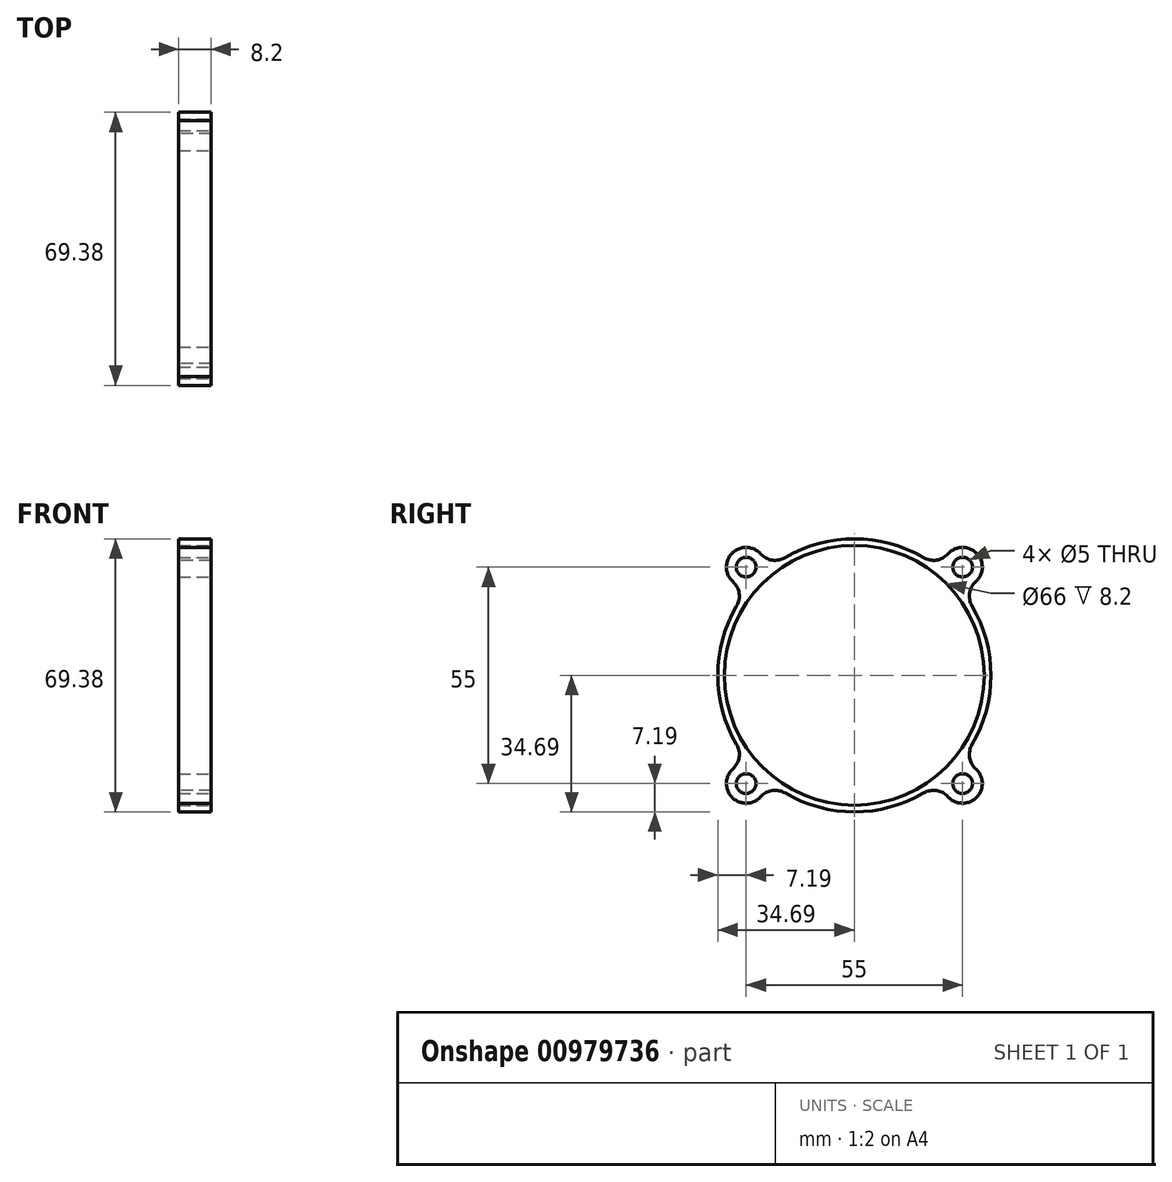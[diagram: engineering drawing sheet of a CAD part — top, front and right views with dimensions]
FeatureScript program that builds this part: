
annotation { "Feature Type Name" : "Feature", "Feature Type Description" : "" }
export const myFeature = defineFeature(function(context is Context, id is Id, definition is map)
    precondition{}
    {
        {
            var Q0;
            Q0=qCreatedBy(makeId("Front.planeOp"),FACE);
            var sketch = newSketch(context, id + "F0", { "sketchPlane" : qUnion([Q0])});
            skLineSegment(sketch, "E0.bottom", {"start": v(20, 40) * mm, "end": v(-20, 40) * mm});
            skLineSegment(sketch, "E0.top", {"start": v(20, -40) * mm, "end": v(-20, -40) * mm});
            skLineSegment(sketch, "E0.left", {"start": v(20, 40) * mm, "end": v(20, -40) * mm});
            skLineSegment(sketch, "E0.right", {"start": v(-20, 40) * mm, "end": v(-20, -40) * mm});
            skPoint(sketch, "E0.middle", {"position": v(0, 0) * mm});
            skSolve(sketch);
        }
        {
            var Q0;
            Q0=qSketchRegion(id+"F0",true);
            extrude(context, id + "F1", {"entities" : qUnion([Q0]), "depth" : 40 * mm, "offsetDistance" : 25 * mm, "hasSecondDirection" : true, "secondDirectionOppositeDirection" : true, "secondDirectionDepth" : 40 * mm});
        }
        {
            var Q0;
            Q0=qCreatedBy(makeId("Front.planeOp"),FACE);
            var sketch = newSketch(context, id + "F2", { "sketchPlane" : qUnion([Q0])});
            skLineSegment(sketch, "E1.left", {"start": v(-17.4, 25) * mm, "end": v(-17.4, 27.1) * mm});
            skPoint(sketch, "E2.center.orphan", {"position": v(0, -57) * mm});
            skPoint(sketch, "E3.start.orphan", {"position": v(-44.08, 0) * mm});
            skArc(sketch, "E4", {"start": v(13.13, 32.04) * mm, "mid": v(0, 33) * mm, "end": v(-13.13, 32.04) * mm});
            skLineSegment(sketch, "E5", {"start": v(17.4, 27.1) * mm, "end": v(17.4, 25) * mm});
            skArc(sketch, "E6", {"start": v(-13.13, 32.04) * mm, "mid": v(-16.18, 30.36) * mm, "end": v(-17.4, 27.1) * mm});
            skArc(sketch, "E7", {"start": v(17.4, 27.1) * mm, "mid": v(16.18, 30.36) * mm, "end": v(13.13, 32.04) * mm});
            skLineSegment(sketch, "E8", {"start": v(-44.08, 0) * mm, "end": v(-17.4, 0) * mm, "construction": true});
            skPoint(sketch, "E9.middle", {"position": v(0, 0) * mm});
            skPoint(sketch, "E9.top.end.orphan", {"position": v(-12.4, -25) * mm});
            skPoint(sketch, "E10.orphan", {"position": v(12.4, -25) * mm});
            skLineSegment(sketch, "E11.trimOffspring", {"start": v(17.4, 0) * mm, "end": v(38.47, 0) * mm, "construction": true});
            skPoint(sketch, "E12.start.orphan", {"position": v(-12.4, 25) * mm});
            skPoint(sketch, "E13.start.orphan", {"position": v(12.4, 25) * mm});
            skLineSegment(sketch, "E14", {"start": v(-17.4, 0) * mm, "end": v(17.4, 0) * mm});
            skLineSegment(sketch, "E15.bottom", {"start": v(-38.47, 25) * mm, "end": v(38.47, 25) * mm});
            skLineSegment(sketch, "E15.left", {"start": v(-38.47, 25) * mm, "end": v(-38.47, 0) * mm});
            skLineSegment(sketch, "E15.right", {"start": v(38.47, 25) * mm, "end": v(38.47, 0) * mm});
            skLineSegment(sketch, "E16", {"start": v(-38.47, 0) * mm, "end": v(38.47, 0) * mm});
            skPoint(sketch, "E15.top.start.orphan", {"position": v(-38.47, -25) * mm});
            skPoint(sketch, "E17.orphan", {"position": v(38.47, -25) * mm});
            skSolve(sketch);
        }
        {
            var Q0;
            Q0=qSketchRegion(id+"F2",true);
            var Q1;
            Q1=sQuery(id+"F2.wireOp",EDGE,"E8");
            revolve(context, id + "F3", {"operationType" : NewBodyOperationType.REMOVE, "surfaceOperationType" : NewSurfaceOperationType.NEW, "entities" : qUnion([Q0]), "axis" : qUnion([Q1]), "revolveType" : RevolveType.FULL});
        }
        {
            var Q0;
            Q0=makeQuery(id+"F1.opExtrude","SWEPT_FACE",FACE,{"disambiguationData":[OSD([sQuery(id+"F0.wireOp",EDGE,"E0.left")])]});
            var sketch = newSketch(context, id + "F4", { "sketchPlane" : qUnion([Q0])});
            skArc(sketch, "E18", {"start": v(-26.27, -22.65) * mm, "mid": v(-31.04, -31.04) * mm, "end": v(-22.65, -26.27) * mm});
            skArc(sketch, "E19", {"start": v(-22.65, 26.27) * mm, "mid": v(-31.04, 31.04) * mm, "end": v(-26.27, 22.65) * mm});
            skArc(sketch, "E20", {"start": v(26.27, 22.65) * mm, "mid": v(31.04, 31.04) * mm, "end": v(22.65, 26.27) * mm});
            skArc(sketch, "E21", {"start": v(22.65, -26.27) * mm, "mid": v(31.04, -31.04) * mm, "end": v(26.27, -22.65) * mm});
            skArc(sketch, "E22", {"start": v(-22.65, -26.27) * mm, "mid": v(0, -34.69) * mm, "end": v(22.65, -26.27) * mm});
            skArc(sketch, "E23.trimOffspring", {"start": v(-26.27, 22.65) * mm, "mid": v(-34.69, 0) * mm, "end": v(-26.27, -22.65) * mm});
            skArc(sketch, "E24.trimOffspring", {"start": v(22.65, 26.27) * mm, "mid": v(0, 34.69) * mm, "end": v(-22.65, 26.27) * mm});
            skArc(sketch, "E25.trimOffspring", {"start": v(26.27, -22.65) * mm, "mid": v(34.69, 0) * mm, "end": v(26.27, 22.65) * mm});
            skCircle(sketch, "E26", {"center": v(0, 0) * mm, "radius": 64.28 * mm});
            skSolve(sketch);
        }
        {
            var Q0;
            Q0=qSketchRegion(id+"F4",true);
            extrude(context, id + "F5", {"entities" : qUnion([Q0]), "operationType" : NewBodyOperationType.REMOVE, "oppositeDirection" : true, "depth" : 40 * mm, "offsetDistance" : 25 * mm});
        }
        {
            var Q0;
            Q0=makeQuery(id+"F5.boolean.opBoolean","MERGE",FACE,{"derivedFrom":[makeQuery(id+"F1.opExtrude","SWEPT_FACE",FACE,{"disambiguationData":[OSD([sQuery(id+"F0.wireOp",EDGE,"E0.left")])]}),makeQuery(id+"F5.opExtrude","CAP_FACE",FACE,{"disambiguationData":[OSD([sQuery(id+"F4.wireOp",EDGE,"E18")])],"isStart":true}),makeQuery(id+"F5.opExtrude","CAP_FACE",FACE,{"disambiguationData":[OSD([sQuery(id+"F4.wireOp",EDGE,"E19")])],"isStart":true}),makeQuery(id+"F5.opExtrude","CAP_FACE",FACE,{"disambiguationData":[OSD([sQuery(id+"F4.wireOp",EDGE,"E20")])],"isStart":true}),makeQuery(id+"F5.opExtrude","CAP_FACE",FACE,{"disambiguationData":[OSD([sQuery(id+"F4.wireOp",EDGE,"E21")])],"isStart":true})]});
            var sketch = newSketch(context, id + "F6", { "sketchPlane" : qUnion([Q0])});
            skCircle(sketch, "E27", {"center": v(-27.5, 27.5) * mm, "radius": 2.5 * mm});
            skCircle(sketch, "E28", {"center": v(27.5, 27.5) * mm, "radius": 2.5 * mm});
            skCircle(sketch, "E29", {"center": v(-27.5, -27.5) * mm, "radius": 2.5 * mm});
            skCircle(sketch, "E30", {"center": v(27.5, -27.5) * mm, "radius": 2.5 * mm});
            skSolve(sketch);
        }
        {
            var Q0;
            Q0=qSketchRegion(id+"F6",true);
            extrude(context, id + "F7", {"entities" : qUnion([Q0]), "operationType" : NewBodyOperationType.REMOVE, "endBound" : BoundingType.THROUGH_ALL, "oppositeDirection" : true, "depth" : 25 * mm, "offsetDistance" : 25 * mm});
        }
        {
            var Q0;
            Q0=qCreatedBy(makeId("Right.planeOp"),FACE);
            var sketch = newSketch(context, id + "F8", { "sketchPlane" : qUnion([Q0])});
            skLineSegment(sketch, "E31.bottom", {"start": v(-50, -50) * mm, "end": v(50, -50) * mm});
            skLineSegment(sketch, "E31.top", {"start": v(-50, 50) * mm, "end": v(50, 50) * mm});
            skLineSegment(sketch, "E31.left", {"start": v(-50, -50) * mm, "end": v(-50, 50) * mm});
            skLineSegment(sketch, "E31.right", {"start": v(50, -50) * mm, "end": v(50, 50) * mm});
            skPoint(sketch, "E31.middle", {"position": v(0, 0) * mm});
            skSolve(sketch);
        }
        {
            var Q0;
            Q0=qSketchRegion(id+"F8",true);
            extrude(context, id + "F9", {"entities" : qUnion([Q0]), "operationType" : NewBodyOperationType.REMOVE, "endBound" : BoundingType.THROUGH_ALL, "oppositeDirection" : true, "depth" : 25 * mm, "offsetDistance" : 25 * mm});
        }
        {
            var Q0;
            Q0=makeQuery(id+"F5.boolean.opBoolean","COPY",EDGE,{"derivedFrom":makeQuery(id+"F5.opExtrude","SWEPT_EDGE",EDGE,{"disambiguationData":[OSD([sQuery(id+"F4.wireOp",EDGE,"E18"),sQuery(id+"F4.wireOp",EDGE,"E23.trimOffspring")])]})});
            var Q1;
            Q1=makeQuery(id+"F5.boolean.opBoolean","COPY",EDGE,{"derivedFrom":makeQuery(id+"F5.opExtrude","SWEPT_EDGE",EDGE,{"disambiguationData":[OSD([sQuery(id+"F4.wireOp",EDGE,"E19"),sQuery(id+"F4.wireOp",EDGE,"E23.trimOffspring")])]})});
            var Q2;
            Q2=makeQuery(id+"F5.boolean.opBoolean","COPY",EDGE,{"derivedFrom":makeQuery(id+"F5.opExtrude","SWEPT_EDGE",EDGE,{"disambiguationData":[OSD([sQuery(id+"F4.wireOp",EDGE,"E20"),sQuery(id+"F4.wireOp",EDGE,"E24.trimOffspring")])]})});
            var Q3;
            Q3=makeQuery(id+"F5.boolean.opBoolean","COPY",EDGE,{"derivedFrom":makeQuery(id+"F5.opExtrude","SWEPT_EDGE",EDGE,{"disambiguationData":[OSD([sQuery(id+"F4.wireOp",EDGE,"E19"),sQuery(id+"F4.wireOp",EDGE,"E24.trimOffspring")])]})});
            var Q4;
            Q4=makeQuery(id+"F5.boolean.opBoolean","COPY",EDGE,{"derivedFrom":makeQuery(id+"F5.opExtrude","SWEPT_EDGE",EDGE,{"disambiguationData":[OSD([sQuery(id+"F4.wireOp",EDGE,"E20"),sQuery(id+"F4.wireOp",EDGE,"E25.trimOffspring")])]})});
            var Q5;
            Q5=makeQuery(id+"F5.boolean.opBoolean","COPY",EDGE,{"derivedFrom":makeQuery(id+"F5.opExtrude","SWEPT_EDGE",EDGE,{"disambiguationData":[OSD([sQuery(id+"F4.wireOp",EDGE,"E21"),sQuery(id+"F4.wireOp",EDGE,"E25.trimOffspring")])]})});
            var Q6;
            Q6=makeQuery(id+"F5.boolean.opBoolean","COPY",EDGE,{"derivedFrom":makeQuery(id+"F5.opExtrude","SWEPT_EDGE",EDGE,{"disambiguationData":[OSD([sQuery(id+"F4.wireOp",EDGE,"E21"),sQuery(id+"F4.wireOp",EDGE,"E22")])]})});
            var Q7;
            Q7=makeQuery(id+"F5.boolean.opBoolean","COPY",EDGE,{"derivedFrom":makeQuery(id+"F5.opExtrude","SWEPT_EDGE",EDGE,{"disambiguationData":[OSD([sQuery(id+"F4.wireOp",EDGE,"E18"),sQuery(id+"F4.wireOp",EDGE,"E22")])]})});
            fillet(context, id + "F10", {"entities" : qUnion([Q0, Q1, Q2, Q3, Q4, Q5, Q6, Q7]), "radius" : 5 * mm, "tangentPropagation" : true, "allowEdgeOverflow" : false});
        }
        {
            var Q0;
            Q0=makeQuery(id+"F9.boolean.opBoolean","COPY",FACE,{"derivedFrom":makeQuery(id+"F9.opExtrude","CAP_FACE",FACE,{"disambiguationData":[OSD([sQuery(id+"F8.wireOp",EDGE,"E31.bottom"),sQuery(id+"F8.wireOp",EDGE,"E31.top"),sQuery(id+"F8.wireOp",EDGE,"E31.left"),sQuery(id+"F8.wireOp",EDGE,"E31.right")])],"isStart":true})});
            extrude(context, id + "F11", {"entities" : qUnion([Q0]), "operationType" : NewBodyOperationType.ADD, "depth" : 8.2 * mm, "offsetDistance" : 25 * mm});
        }
        {
            var Q0;
            Q0=makeQuery(id+"F1.opExtrude","SWEPT_FACE",FACE,{"disambiguationData":[OSD([sQuery(id+"F0.wireOp",EDGE,"E0.left")])]});
            extrude(context, id + "F12", {"entities" : qUnion([Q0]), "operationType" : NewBodyOperationType.REMOVE, "oppositeDirection" : true, "depth" : 20 * mm, "offsetDistance" : 25 * mm});
        }
    });
